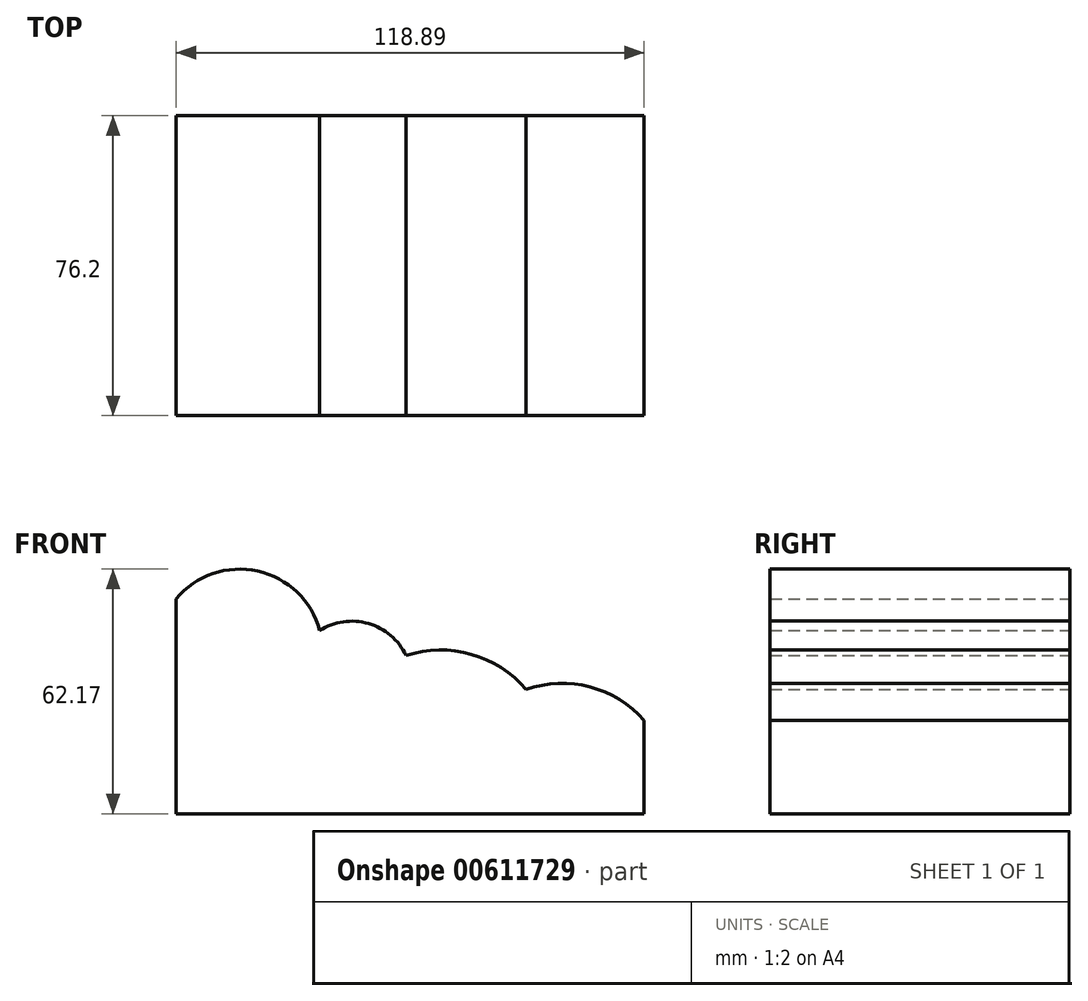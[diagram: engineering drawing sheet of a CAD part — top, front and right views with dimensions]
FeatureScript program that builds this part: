
annotation { "Feature Type Name" : "Feature", "Feature Type Description" : "" }
export const myFeature = defineFeature(function(context is Context, id is Id, definition is map)
    precondition{}
    {
        {
            var Q0;
            Q0=qCreatedBy(makeId("Front.planeOp"),FACE);
            var sketch = newSketch(context, id + "F0", { "sketchPlane" : qUnion([Q0])});
            skLineSegment(sketch, "E0.bottom", {"start": v(0, 0) * mm, "end": v(118.9, 0) * mm});
            skLineSegment(sketch, "E0.top", {"start": v(0, 65.28) * mm, "end": v(118.9, 65.28) * mm});
            skLineSegment(sketch, "E0.left", {"start": v(0, 0) * mm, "end": v(0, 65.28) * mm});
            skLineSegment(sketch, "E0.right", {"start": v(118.9, 0) * mm, "end": v(118.9, 65.28) * mm});
            skSolve(sketch);
        }
        {
            var Q0;
            Q0=makeQuery(id+"F0.imprint","IMPRINT",FACE,{"disambiguationData":[TD([[makeQuery(id+"F0.imprint","IMPRINT",EDGE,{"derivedFrom":sQuery(id+"F0.wireOp",EDGE,"E0.bottom")}),1.0]])]});
            extrude(context, id + "F1", {"entities" : qUnion([Q0]), "depth" : 76.2 * mm, "offsetDistance" : 25.4 * mm});
        }
        {
            var Q0;
            Q0=qCreatedBy(makeId("Front.planeOp"),FACE);
            var sketch = newSketch(context, id + "F2", { "sketchPlane" : qUnion([Q0])});
            skArc(sketch, "E1", {"start": v(119.76, 22.63) * mm, "mid": v(105.78, 32.07) * mm, "end": v(88.92, 31.56) * mm});
            skArc(sketch, "E2", {"start": v(88.92, 31.56) * mm, "mid": v(74.96, 40.55) * mm, "end": v(58.37, 40.2) * mm});
            skArc(sketch, "E3", {"start": v(58.37, 40.2) * mm, "mid": v(48.85, 48.34) * mm, "end": v(36.46, 46.55) * mm});
            skArc(sketch, "E4", {"start": v(36.46, 46.55) * mm, "mid": v(20.69, 61.68) * mm, "end": v(0, 54.62) * mm});
            skLineSegment(sketch, "E5", {"start": v(119.76, 22.63) * mm, "end": v(123.44, 71.19) * mm});
            skLineSegment(sketch, "E6", {"start": v(123.44, 71.19) * mm, "end": v(-3.07, 71.19) * mm});
            skLineSegment(sketch, "E7", {"start": v(-3.07, 71.19) * mm, "end": v(0, 54.62) * mm});
            skSolve(sketch);
        }
        {
            var Q0;
            Q0=makeQuery(id+"F2.imprint","IMPRINT",FACE,{"disambiguationData":[TD([[makeQuery(id+"F2.imprint","IMPRINT",EDGE,{"derivedFrom":sQuery(id+"F2.wireOp",EDGE,"E1")}),-1.0]])]});
            extrude(context, id + "F3", {"entities" : qUnion([Q0]), "operationType" : NewBodyOperationType.REMOVE, "depth" : 152.4 * mm, "offsetDistance" : 25.4 * mm});
        }
    });
